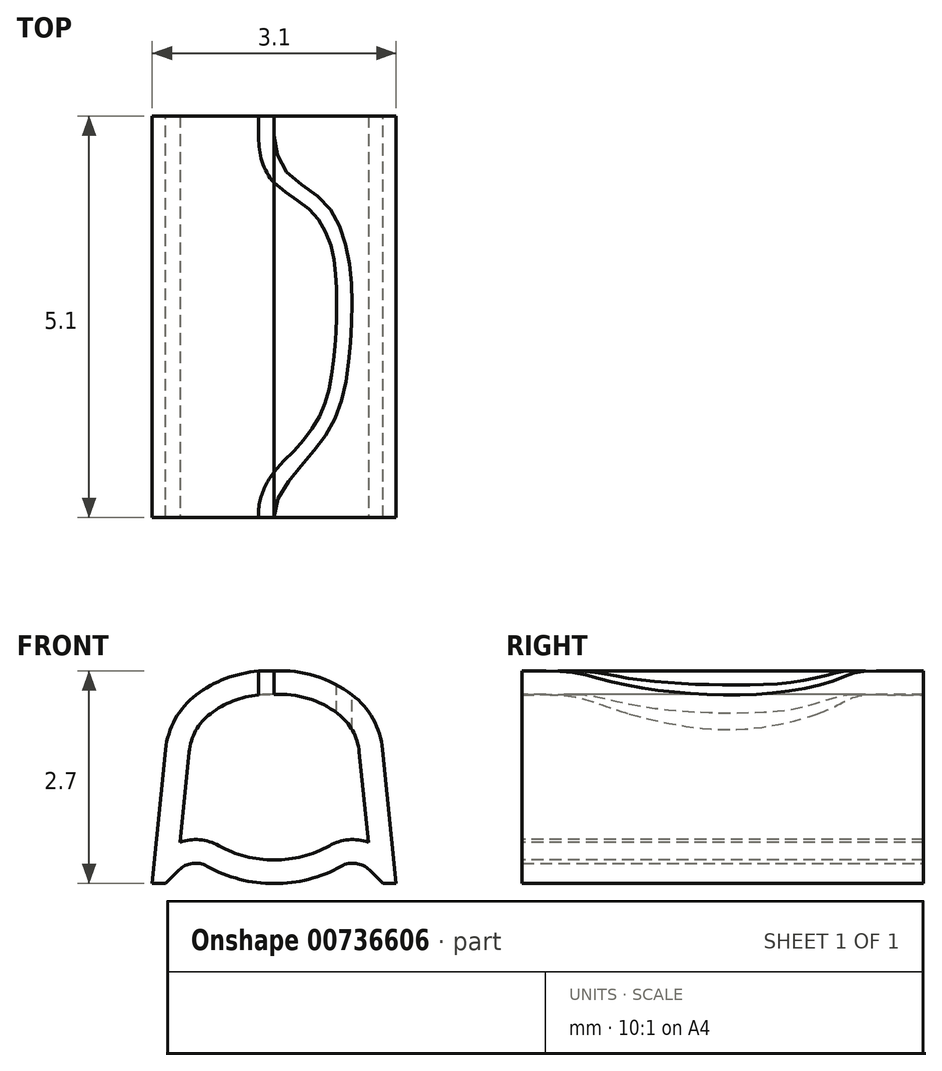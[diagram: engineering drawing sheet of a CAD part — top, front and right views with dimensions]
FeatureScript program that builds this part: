
annotation { "Feature Type Name" : "Feature", "Feature Type Description" : "" }
export const myFeature = defineFeature(function(context is Context, id is Id, definition is map)
    precondition{}
    {
        {
            var Q0;
            Q0=qCreatedBy(makeId("Front.planeOp"),FACE);
            var sketch = newSketch(context, id + "F0", { "sketchPlane" : qUnion([Q0])});
            skLineSegment(sketch, "E0.bottom", {"start": v(1.55, -1.35) * mm, "end": v(-1.55, -1.35) * mm, "construction": true});
            skLineSegment(sketch, "E0.top", {"start": v(1.55, 1.35) * mm, "end": v(-1.55, 1.35) * mm, "construction": true});
            skLineSegment(sketch, "E0.left", {"start": v(1.55, -1.35) * mm, "end": v(1.55, 1.35) * mm, "construction": true});
            skLineSegment(sketch, "E0.right", {"start": v(-1.55, -1.35) * mm, "end": v(-1.55, 1.35) * mm, "construction": true});
            skPoint(sketch, "E0.middle", {"position": v(0, 0) * mm});
            skLineSegment(sketch, "E1", {"start": v(-1.55, -1.35) * mm, "end": v(-1.38, -1.35) * mm});
            skLineSegment(sketch, "E2", {"start": v(-1.38, -1.35) * mm, "end": v(-1.21, -1.18) * mm});
            skLineSegment(sketch, "E3", {"start": v(0, 1.35) * mm, "end": v(0, -1.35) * mm, "construction": true});
            skArc(sketch, "E4", {"start": v(-0.85, -1.13) * mm, "mid": v(-0.44, -1.3) * mm, "end": v(0, -1.35) * mm});
            skLineSegment(sketch, "E5", {"start": v(-1.55, -1.35) * mm, "end": v(-1.38, 0.35) * mm});
            skArc(sketch, "E6", {"start": v(0, 1.35) * mm, "mid": v(-0.52, 1.29) * mm, "end": v(-0.99, 1.05) * mm});
            skPoint(sketch, "E7.visualSharp", {"position": v(-1.35, 0.65) * mm});
            skArc(sketch, "E7.filletArc", {"start": v(-0.99, 1.05) * mm, "mid": v(-1.26, 0.74) * mm, "end": v(-1.38, 0.35) * mm});
            skPoint(sketch, "E8.visualSharp", {"position": v(-1.04, -1) * mm});
            skArc(sketch, "E8.filletArc", {"start": v(-0.85, -1.13) * mm, "mid": v(-1.04, -1.1) * mm, "end": v(-1.21, -1.18) * mm});
            skArc(sketch, "E9.MirrorCS", {"start": v(0, 1.35) * mm, "mid": v(0.52, 1.29) * mm, "end": v(0.99, 1.05) * mm});
            skArc(sketch, "E10.MirrorCS", {"start": v(0.99, 1.05) * mm, "mid": v(1.26, 0.74) * mm, "end": v(1.38, 0.35) * mm});
            skLineSegment(sketch, "E11.MirrorCS", {"start": v(1.55, -1.35) * mm, "end": v(1.38, 0.35) * mm});
            skLineSegment(sketch, "E12.MirrorCS", {"start": v(1.38, -1.35) * mm, "end": v(1.21, -1.18) * mm});
            skArc(sketch, "E13.MirrorCS", {"start": v(0.85, -1.13) * mm, "mid": v(1.04, -1.1) * mm, "end": v(1.21, -1.18) * mm});
            skArc(sketch, "E14.MirrorCS", {"start": v(0.85, -1.13) * mm, "mid": v(0.44, -1.3) * mm, "end": v(0, -1.35) * mm});
            skLineSegment(sketch, "E15", {"start": v(1.38, -1.35) * mm, "end": v(1.55, -1.35) * mm});
            skSolve(sketch);
        }
        {
            var Q0;
            Q0 = qSketchRegion(id + "F0", true);
            extrude(context, id + "F1", {"entities" : qUnion([Q0]), "depth" : 5.1 * mm, "offsetDistance" : 25 * mm, "symmetric" : true});
        }
        {
            var Q0;
            Q0=makeQuery(id+"F1.opExtrude","CAP_FACE",FACE,{"disambiguationData":[OSD([sQuery(id+"F0.wireOp",EDGE,"E1"),sQuery(id+"F0.wireOp",EDGE,"E2"),sQuery(id+"F0.wireOp",EDGE,"E4"),sQuery(id+"F0.wireOp",EDGE,"E5"),sQuery(id+"F0.wireOp",EDGE,"E6"),sQuery(id+"F0.wireOp",EDGE,"E7.filletArc"),sQuery(id+"F0.wireOp",EDGE,"E8.filletArc"),sQuery(id+"F0.wireOp",EDGE,"E9.MirrorCS"),sQuery(id+"F0.wireOp",EDGE,"E10.MirrorCS"),sQuery(id+"F0.wireOp",EDGE,"E11.MirrorCS"),sQuery(id+"F0.wireOp",EDGE,"E12.MirrorCS"),sQuery(id+"F0.wireOp",EDGE,"E13.MirrorCS"),sQuery(id+"F0.wireOp",EDGE,"E14.MirrorCS"),sQuery(id+"F0.wireOp",EDGE,"E15")])],"isStart":false});
            var sketch = newSketch(context, id + "F2", { "sketchPlane" : qUnion([Q0])});
            skArc(sketch, "E16.0", {"start": v(-0.7, -0.87) * mm, "mid": v(-0.36, -1) * mm, "end": v(0, -1.05) * mm});
            skArc(sketch, "E16.1", {"start": v(-1.2, -0.83) * mm, "mid": v(-0.94, -0.8) * mm, "end": v(-0.7, -0.87) * mm});
            skArc(sketch, "E16.2", {"start": v(0, -1.05) * mm, "mid": v(0.36, -1) * mm, "end": v(0.7, -0.87) * mm});
            skLineSegment(sketch, "E16.3", {"start": v(-1.08, 0.32) * mm, "end": v(-1.2, -0.83) * mm});
            skArc(sketch, "E16.4", {"start": v(-0.8, 0.8) * mm, "mid": v(-1, 0.6) * mm, "end": v(-1.08, 0.32) * mm});
            skArc(sketch, "E16.5", {"start": v(0, 1.05) * mm, "mid": v(-0.43, 1) * mm, "end": v(-0.8, 0.8) * mm});
            skArc(sketch, "E16.6", {"start": v(0.7, -0.87) * mm, "mid": v(0.94, -0.8) * mm, "end": v(1.2, -0.83) * mm});
            skLineSegment(sketch, "E16.7", {"start": v(1.2, -0.83) * mm, "end": v(1.08, 0.32) * mm});
            skArc(sketch, "E16.8", {"start": v(1.08, 0.32) * mm, "mid": v(1, 0.6) * mm, "end": v(0.8, 0.8) * mm});
            skArc(sketch, "E16.9", {"start": v(0.8, 0.8) * mm, "mid": v(0.43, 1) * mm, "end": v(0, 1.05) * mm});
            skSolve(sketch);
        }
        {
            var Q0;
            Q0 = qSketchRegion(id + "F2", true);
            extrude(context, id + "F3", {"entities" : qUnion([Q0]), "operationType" : NewBodyOperationType.REMOVE, "oppositeDirection" : true, "depth" : 25 * mm, "offsetDistance" : 25 * mm});
        }
        {
            var Q0;
            Q0=qCreatedBy(makeId("Top.planeOp"),FACE);
            var sketch = newSketch(context, id + "F4", { "sketchPlane" : qUnion([Q0])});
            skLineSegment(sketch, "E17", {"start": v(0, 2.55) * mm, "end": v(0, -2.55) * mm, "construction": true});
            skFitSpline(sketch, "E18", {"points": [v(0, 2.55) * mm, v(0.11, 1.9) * mm, v(0.7, 1.38) * mm, v(0.99, 0) * mm, v(0.7, -1.44) * mm, v(0.19, -2.07) * mm, v(0, -2.55) * mm], "startDerivative": vector(0, -5.24) * mm, "endDerivative": vector(0, -3.94) * mm});
            skLineSegment(sketch, "E19", {"start": v(0.7, 2.55) * mm, "end": v(0.7, -2.55) * mm, "construction": true});
            skLineSegment(sketch, "E20", {"start": v(0, 0) * mm, "end": v(1.56, 0) * mm, "construction": true});
            skFitSpline(sketch, "E21.0", {"points": [v(-0.2, 2.55) * mm, v(-0.2, 2.44) * mm, v(-0.2, 2.28) * mm, v(-0.17, 2.05) * mm, v(-0.12, 1.87) * mm, v(0, 1.7) * mm, v(0.13, 1.6) * mm, v(0.27, 1.5) * mm, v(0.4, 1.4) * mm, v(0.5, 1.31) * mm, v(0.6, 1.18) * mm, v(0.72, 0.91) * mm, v(0.78, 0.5) * mm, v(0.8, 0.04) * mm, v(0.77, -0.42) * mm, v(0.7, -0.85) * mm, v(0.6, -1.22) * mm, v(0.45, -1.49) * mm, v(0.24, -1.71) * mm, v(0.02, -1.94) * mm, v(-0.15, -2.22) * mm, v(-0.2, -2.44) * mm, v(-0.2, -2.55) * mm]});
            skLineSegment(sketch, "E22", {"start": v(-0.2, 2.55) * mm, "end": v(0, 2.55) * mm});
            skLineSegment(sketch, "E23", {"start": v(-0.2, -2.55) * mm, "end": v(0, -2.55) * mm});
            skSolve(sketch);
        }
        {
            var Q0;
            Q0 = qSketchRegion(id + "F4", true);
            extrude(context, id + "F5", {"entities" : qUnion([Q0]), "operationType" : NewBodyOperationType.REMOVE, "depth" : 25 * mm, "offsetDistance" : 25 * mm});
        }
    });
